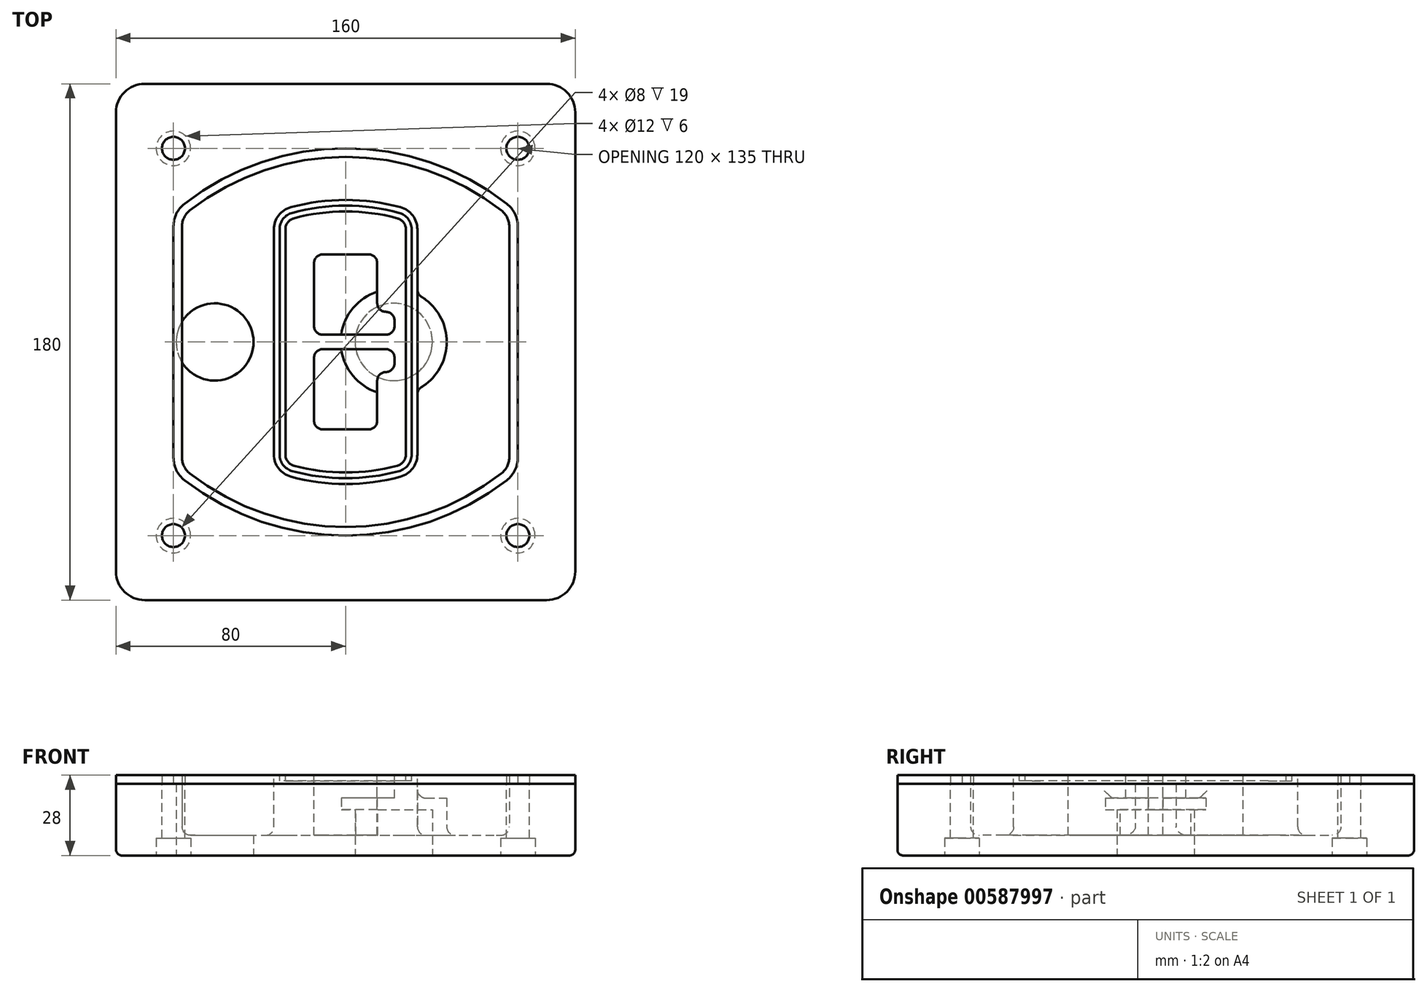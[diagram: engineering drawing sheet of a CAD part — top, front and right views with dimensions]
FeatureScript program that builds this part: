
annotation { "Feature Type Name" : "Feature", "Feature Type Description" : "" }
export const myFeature = defineFeature(function(context is Context, id is Id, definition is map)
    precondition{}
    {
        {
            var Q0;
            Q0=qCreatedBy(makeId("Top.planeOp"),FACE);
            var sketch = newSketch(context, id + "F0", { "sketchPlane" : qUnion([Q0])});
            skPoint(sketch, "E0.rect.middle", {"position": v(0, 0) * mm});
            skLineSegment(sketch, "E1.bottom", {"start": v(-70, -90) * mm, "end": v(70, -90) * mm});
            skLineSegment(sketch, "E1.top", {"start": v(-70, 90) * mm, "end": v(70, 90) * mm});
            skLineSegment(sketch, "E1.left", {"start": v(-80, -80) * mm, "end": v(-80, 80) * mm});
            skLineSegment(sketch, "E1.right", {"start": v(80, -80) * mm, "end": v(80, 80) * mm});
            skLineSegment(sketch, "E2", {"start": v(-80, 90) * mm, "end": v(80, -90) * mm, "construction": true});
            skLineSegment(sketch, "E3", {"start": v(80, 90) * mm, "end": v(-80, -90) * mm, "construction": true});
            skCircle(sketch, "E4", {"center": v(-60, 67.5) * mm, "radius": 4 * mm});
            skCircle(sketch, "E5", {"center": v(60, 67.5) * mm, "radius": 4 * mm});
            skCircle(sketch, "E6", {"center": v(60, -67.5) * mm, "radius": 4 * mm});
            skCircle(sketch, "E7", {"center": v(-60, -67.5) * mm, "radius": 4 * mm});
            skLineSegment(sketch, "E8", {"start": v(-60, 67.5) * mm, "end": v(60, 67.5) * mm, "construction": true});
            skLineSegment(sketch, "E9", {"start": v(60, 67.5) * mm, "end": v(60, -67.5) * mm, "construction": true});
            skLineSegment(sketch, "E10", {"start": v(60, -67.5) * mm, "end": v(-60, -67.5) * mm, "construction": true});
            skLineSegment(sketch, "E11", {"start": v(-60, -67.5) * mm, "end": v(-60, 67.5) * mm, "construction": true});
            skLineSegment(sketch, "E12", {"start": v(-60, 40.3) * mm, "end": v(-60, -40.3) * mm});
            skLineSegment(sketch, "E13", {"start": v(60, 40.3) * mm, "end": v(60, -40.3) * mm});
            skArc(sketch, "E14", {"start": v(56.15, 48.18) * mm, "mid": v(0, 67.5) * mm, "end": v(-56.15, 48.18) * mm});
            skArc(sketch, "E15", {"start": v(-56.15, -48.18) * mm, "mid": v(0, -67.5) * mm, "end": v(56.15, -48.18) * mm});
            skLineSegment(sketch, "E16", {"start": v(-60, 0) * mm, "end": v(60, 0) * mm, "construction": true});
            skPoint(sketch, "E17.visualSharp", {"position": v(-60, -45) * mm});
            skArc(sketch, "E17.filletArc", {"start": v(-60, -40.3) * mm, "mid": v(-58.99, -44.68) * mm, "end": v(-56.15, -48.18) * mm});
            skPoint(sketch, "E18.visualSharp", {"position": v(-60, 45) * mm});
            skArc(sketch, "E18.filletArc", {"start": v(-56.15, 48.18) * mm, "mid": v(-58.99, 44.68) * mm, "end": v(-60, 40.3) * mm});
            skPoint(sketch, "E19.visualSharp", {"position": v(60, 45) * mm});
            skArc(sketch, "E19.filletArc", {"start": v(60, 40.3) * mm, "mid": v(58.99, 44.68) * mm, "end": v(56.15, 48.18) * mm});
            skPoint(sketch, "E20.visualSharp", {"position": v(60, -45) * mm});
            skArc(sketch, "E20.filletArc", {"start": v(56.15, -48.18) * mm, "mid": v(58.99, -44.68) * mm, "end": v(60, -40.3) * mm});
            skPoint(sketch, "E21.visualSharp", {"position": v(-80, 90) * mm});
            skArc(sketch, "E21.filletArc", {"start": v(-70, 90) * mm, "mid": v(-77.07, 87.07) * mm, "end": v(-80, 80) * mm});
            skPoint(sketch, "E22.visualSharp", {"position": v(80, 90) * mm});
            skArc(sketch, "E22.filletArc", {"start": v(80, 80) * mm, "mid": v(77.07, 87.07) * mm, "end": v(70, 90) * mm});
            skPoint(sketch, "E23.visualSharp", {"position": v(80, -90) * mm});
            skArc(sketch, "E23.filletArc", {"start": v(70, -90) * mm, "mid": v(77.07, -87.07) * mm, "end": v(80, -80) * mm});
            skPoint(sketch, "E24.visualSharp", {"position": v(-80, -90) * mm});
            skArc(sketch, "E24.filletArc", {"start": v(-80, -80) * mm, "mid": v(-77.07, -87.07) * mm, "end": v(-70, -90) * mm});
            skArc(sketch, "E25.0", {"start": v(57, 40.3) * mm, "mid": v(56.3, 43.36) * mm, "end": v(54.3, 45.81) * mm});
            skLineSegment(sketch, "E25.1", {"start": v(57, 40.3) * mm, "end": v(57, -40.3) * mm});
            skArc(sketch, "E25.2", {"start": v(54.3, -45.81) * mm, "mid": v(56.3, -43.36) * mm, "end": v(57, -40.3) * mm});
            skArc(sketch, "E25.3", {"start": v(-54.3, -45.81) * mm, "mid": v(0, -64.5) * mm, "end": v(54.3, -45.81) * mm});
            skArc(sketch, "E25.4", {"start": v(-57, -40.3) * mm, "mid": v(-56.3, -43.36) * mm, "end": v(-54.3, -45.81) * mm});
            skArc(sketch, "E25.5", {"start": v(54.3, 45.81) * mm, "mid": v(0, 64.5) * mm, "end": v(-54.3, 45.81) * mm});
            skLineSegment(sketch, "E25.6", {"start": v(-57, 40.3) * mm, "end": v(-57, -40.3) * mm});
            skArc(sketch, "E25.7", {"start": v(-54.3, 45.81) * mm, "mid": v(-56.3, 43.36) * mm, "end": v(-57, 40.3) * mm});
            skArc(sketch, "E26.0", {"start": v(-58.62, 51.33) * mm, "mid": v(-62.58, 46.43) * mm, "end": v(-64, 40.3) * mm});
            skArc(sketch, "E26.1", {"start": v(58.62, 51.33) * mm, "mid": v(0, 71.5) * mm, "end": v(-58.62, 51.33) * mm});
            skArc(sketch, "E26.2", {"start": v(64, 40.3) * mm, "mid": v(62.58, 46.43) * mm, "end": v(58.62, 51.33) * mm});
            skLineSegment(sketch, "E26.3", {"start": v(64, 40.3) * mm, "end": v(64, -40.3) * mm});
            skArc(sketch, "E26.4", {"start": v(58.62, -51.33) * mm, "mid": v(62.58, -46.43) * mm, "end": v(64, -40.3) * mm});
            skLineSegment(sketch, "E26.5", {"start": v(-64, 40.3) * mm, "end": v(-64, -40.3) * mm});
            skArc(sketch, "E26.6", {"start": v(-58.62, -51.33) * mm, "mid": v(0, -71.5) * mm, "end": v(58.62, -51.33) * mm});
            skArc(sketch, "E26.7", {"start": v(-64, -40.3) * mm, "mid": v(-62.58, -46.43) * mm, "end": v(-58.62, -51.33) * mm});
            skSolve(sketch);
        }
        {
            var Q0;
            Q0=makeQuery(id+"F0.imprint","IMPRINT",FACE,{"disambiguationData":[TD([[makeQuery(id+"F0.imprint","IMPRINT",EDGE,{"derivedFrom":sQuery(id+"F0.wireOp",EDGE,"E1.bottom")}),1.0]])]});
            var Q1;
            Q1=makeQuery(id+"F0.imprint","IMPRINT",FACE,{"disambiguationData":[TD([[makeQuery(id+"F0.imprint","IMPRINT",EDGE,{"derivedFrom":sQuery(id+"F0.wireOp",EDGE,"E12")}),1.0]])]});
            var Q2;
            Q2=makeQuery(id+"F0.imprint","IMPRINT",FACE,{"disambiguationData":[TD([[makeQuery(id+"F0.imprint","IMPRINT",EDGE,{"derivedFrom":sQuery(id+"F0.wireOp",EDGE,"E25.0")}),1.0]])]});
            var Q3;
            Q3=makeQuery(id+"F0.imprint","IMPRINT",FACE,{"disambiguationData":[TD([[makeQuery(id+"F0.imprint","IMPRINT",EDGE,{"derivedFrom":sQuery(id+"F0.wireOp",EDGE,"E12")}),-1.0]])]});
            extrude(context, id + "F1", {"entities" : qUnion([Q0, Q1, Q2, Q3]), "oppositeDirection" : true, "depth" : 25 * mm});
        }
        {
            var Q0;
            Q0=makeQuery(id+"F0.imprint","IMPRINT",FACE,{"disambiguationData":[TD([[makeQuery(id+"F0.imprint","IMPRINT",EDGE,{"derivedFrom":sQuery(id+"F0.wireOp",EDGE,"E12")}),1.0]])]});
            extrude(context, id + "F2", {"entities" : qUnion([Q0]), "operationType" : NewBodyOperationType.ADD, "depth" : 3 * mm});
        }
        {
            var Q0;
            Q0=makeQuery(id+"F0.imprint","IMPRINT",FACE,{"disambiguationData":[TD([[makeQuery(id+"F0.imprint","IMPRINT",EDGE,{"derivedFrom":sQuery(id+"F0.wireOp",EDGE,"E25.0")}),1.0]])]});
            extrude(context, id + "F3", {"entities" : qUnion([Q0]), "operationType" : NewBodyOperationType.REMOVE, "oppositeDirection" : true, "depth" : 18 * mm});
        }
        {
            var Q0;
            Q0=makeQuery(id+"F2.opExtrude","CAP_FACE",FACE,{"disambiguationData":[OSD([sQuery(id+"F0.wireOp",EDGE,"E12"),sQuery(id+"F0.wireOp",EDGE,"E13"),sQuery(id+"F0.wireOp",EDGE,"E14"),sQuery(id+"F0.wireOp",EDGE,"E15"),sQuery(id+"F0.wireOp",EDGE,"E17.filletArc"),sQuery(id+"F0.wireOp",EDGE,"E18.filletArc"),sQuery(id+"F0.wireOp",EDGE,"E19.filletArc"),sQuery(id+"F0.wireOp",EDGE,"E20.filletArc"),sQuery(id+"F0.wireOp",EDGE,"E25.0"),sQuery(id+"F0.wireOp",EDGE,"E25.1"),sQuery(id+"F0.wireOp",EDGE,"E25.2"),sQuery(id+"F0.wireOp",EDGE,"E25.3"),sQuery(id+"F0.wireOp",EDGE,"E25.4"),sQuery(id+"F0.wireOp",EDGE,"E25.5"),sQuery(id+"F0.wireOp",EDGE,"E25.6"),sQuery(id+"F0.wireOp",EDGE,"E25.7")])],"isStart":false});
            var sketch = newSketch(context, id + "F4", { "sketchPlane" : qUnion([Q0])});
            skArc(sketch, "E27.0", {"start": v(-19.08, -46.97) * mm, "mid": v(0, -49.5) * mm, "end": v(19.08, -46.97) * mm});
            skArc(sketch, "E28.0", {"start": v(19.08, 46.97) * mm, "mid": v(0, 49.5) * mm, "end": v(-19.08, 46.97) * mm});
            skLineSegment(sketch, "E29", {"start": v(-25, 39.25) * mm, "end": v(-25, -39.25) * mm});
            skLineSegment(sketch, "E30", {"start": v(25, 39.25) * mm, "end": v(25, -39.25) * mm});
            skLineSegment(sketch, "E31", {"start": v(-25, 45.1) * mm, "end": v(25, 45.1) * mm, "construction": true});
            skLineSegment(sketch, "E32", {"start": v(-25, -45.1) * mm, "end": v(25, -45.1) * mm, "construction": true});
            skPoint(sketch, "E33.visualSharp", {"position": v(-25, 45.1) * mm});
            skArc(sketch, "E33.filletArc", {"start": v(-19.08, 46.97) * mm, "mid": v(-23.35, 44.11) * mm, "end": v(-25, 39.25) * mm});
            skPoint(sketch, "E34.visualSharp", {"position": v(25, 45.1) * mm});
            skArc(sketch, "E34.filletArc", {"start": v(25, 39.25) * mm, "mid": v(23.35, 44.11) * mm, "end": v(19.08, 46.97) * mm});
            skPoint(sketch, "E35.visualSharp", {"position": v(25, -45.1) * mm});
            skArc(sketch, "E35.filletArc", {"start": v(19.08, -46.97) * mm, "mid": v(23.35, -44.11) * mm, "end": v(25, -39.25) * mm});
            skPoint(sketch, "E36.visualSharp", {"position": v(-25, -45.1) * mm});
            skArc(sketch, "E36.filletArc", {"start": v(-25, -39.25) * mm, "mid": v(-23.35, -44.11) * mm, "end": v(-19.08, -46.97) * mm});
            skArc(sketch, "E37.0", {"start": v(54.3, 45.81) * mm, "mid": v(0, 64.5) * mm, "end": v(-54.3, 45.81) * mm});
            skArc(sketch, "E37.1", {"start": v(-54.3, 45.81) * mm, "mid": v(-56.3, 43.36) * mm, "end": v(-57, 40.3) * mm});
            skLineSegment(sketch, "E37.2", {"start": v(-57, 40.3) * mm, "end": v(-57, -40.3) * mm});
            skArc(sketch, "E37.3", {"start": v(-57, -40.3) * mm, "mid": v(-56.3, -43.36) * mm, "end": v(-54.3, -45.81) * mm});
            skArc(sketch, "E37.4", {"start": v(-54.3, -45.81) * mm, "mid": v(0, -64.5) * mm, "end": v(54.3, -45.81) * mm});
            skArc(sketch, "E37.5", {"start": v(54.3, -45.81) * mm, "mid": v(56.3, -43.36) * mm, "end": v(57, -40.3) * mm});
            skLineSegment(sketch, "E37.6", {"start": v(57, 40.3) * mm, "end": v(57, -40.3) * mm});
            skArc(sketch, "E37.7", {"start": v(57, 40.3) * mm, "mid": v(56.3, 43.36) * mm, "end": v(54.3, 45.81) * mm});
            skLineSegment(sketch, "E38.0", {"start": v(23, 39.25) * mm, "end": v(23, -39.25) * mm});
            skArc(sketch, "E38.1", {"start": v(18.56, -45.04) * mm, "mid": v(21.76, -42.9) * mm, "end": v(23, -39.25) * mm});
            skArc(sketch, "E38.2", {"start": v(-18.56, -45.04) * mm, "mid": v(0, -47.5) * mm, "end": v(18.56, -45.04) * mm});
            skArc(sketch, "E38.3", {"start": v(-23, -39.25) * mm, "mid": v(-21.76, -42.9) * mm, "end": v(-18.56, -45.04) * mm});
            skLineSegment(sketch, "E38.4", {"start": v(-23, 39.25) * mm, "end": v(-23, -39.25) * mm});
            skArc(sketch, "E38.5", {"start": v(23, 39.25) * mm, "mid": v(21.76, 42.9) * mm, "end": v(18.56, 45.04) * mm});
            skArc(sketch, "E38.6", {"start": v(-18.56, 45.04) * mm, "mid": v(-21.76, 42.9) * mm, "end": v(-23, 39.25) * mm});
            skArc(sketch, "E38.7", {"start": v(18.56, 45.04) * mm, "mid": v(0, 47.5) * mm, "end": v(-18.56, 45.04) * mm});
            skArc(sketch, "E39.0", {"start": v(21, 39.25) * mm, "mid": v(20.18, 41.68) * mm, "end": v(18.04, 43.1) * mm});
            skLineSegment(sketch, "E39.1", {"start": v(21, 39.25) * mm, "end": v(21, -39.25) * mm});
            skArc(sketch, "E39.2", {"start": v(18.04, -43.1) * mm, "mid": v(20.18, -41.68) * mm, "end": v(21, -39.25) * mm});
            skArc(sketch, "E39.3", {"start": v(-18.04, -43.1) * mm, "mid": v(0, -45.5) * mm, "end": v(18.04, -43.1) * mm});
            skArc(sketch, "E39.4", {"start": v(-21, -39.25) * mm, "mid": v(-20.18, -41.68) * mm, "end": v(-18.04, -43.1) * mm});
            skArc(sketch, "E39.5", {"start": v(18.04, 43.1) * mm, "mid": v(0, 45.5) * mm, "end": v(-18.04, 43.1) * mm});
            skLineSegment(sketch, "E39.6", {"start": v(-21, 39.25) * mm, "end": v(-21, -39.25) * mm});
            skArc(sketch, "E39.7", {"start": v(-18.04, 43.1) * mm, "mid": v(-20.18, 41.68) * mm, "end": v(-21, 39.25) * mm});
            skLineSegment(sketch, "E40", {"start": v(-25, 0) * mm, "end": v(25, 0) * mm, "construction": true});
            skLineSegment(sketch, "E41", {"start": v(-11, 5.5) * mm, "end": v(-11, 27.5) * mm});
            skLineSegment(sketch, "E42", {"start": v(-8, 30.5) * mm, "end": v(8, 30.5) * mm});
            skLineSegment(sketch, "E43", {"start": v(11, 27.5) * mm, "end": v(11, 13.5) * mm});
            skLineSegment(sketch, "E44", {"start": v(14, 10.5) * mm, "end": v(14, 10.5) * mm});
            skLineSegment(sketch, "E45", {"start": v(17, 7.5) * mm, "end": v(17, 5.5) * mm});
            skLineSegment(sketch, "E46", {"start": v(14, 2.5) * mm, "end": v(-8, 2.5) * mm});
            skPoint(sketch, "E47.visualSharp", {"position": v(-11, 30.5) * mm});
            skArc(sketch, "E47.filletArc", {"start": v(-8, 30.5) * mm, "mid": v(-10.12, 29.62) * mm, "end": v(-11, 27.5) * mm});
            skPoint(sketch, "E48.visualSharp", {"position": v(11, 30.5) * mm});
            skArc(sketch, "E48.filletArc", {"start": v(11, 27.5) * mm, "mid": v(10.12, 29.62) * mm, "end": v(8, 30.5) * mm});
            skPoint(sketch, "E49.visualSharp", {"position": v(11, 10.5) * mm});
            skArc(sketch, "E49.filletArc", {"start": v(11, 13.5) * mm, "mid": v(11.88, 11.38) * mm, "end": v(14, 10.5) * mm});
            skPoint(sketch, "E50.visualSharp", {"position": v(17, 10.5) * mm});
            skArc(sketch, "E50.filletArc", {"start": v(17, 7.5) * mm, "mid": v(16.12, 9.62) * mm, "end": v(14, 10.5) * mm});
            skPoint(sketch, "E51.visualSharp", {"position": v(17, 2.5) * mm});
            skArc(sketch, "E51.filletArc", {"start": v(14, 2.5) * mm, "mid": v(16.12, 3.38) * mm, "end": v(17, 5.5) * mm});
            skPoint(sketch, "E52.visualSharp", {"position": v(-11, 2.5) * mm});
            skArc(sketch, "E52.filletArc", {"start": v(-11, 5.5) * mm, "mid": v(-10.12, 3.38) * mm, "end": v(-8, 2.5) * mm});
            skLineSegment(sketch, "E53.0.MirrorCS", {"start": v(14, -2.5) * mm, "end": v(-8, -2.5) * mm});
            skArc(sketch, "E54.0.MirrorCS", {"start": v(-11, -5.5) * mm, "mid": v(-10.12, -3.38) * mm, "end": v(-8, -2.5) * mm});
            skLineSegment(sketch, "E55.0.MirrorCS", {"start": v(-11, -5.5) * mm, "end": v(-11, -27.5) * mm});
            skArc(sketch, "E56.0.MirrorCS", {"start": v(-8, -30.5) * mm, "mid": v(-10.12, -29.62) * mm, "end": v(-11, -27.5) * mm});
            skLineSegment(sketch, "E57.0.MirrorCS", {"start": v(-8, -30.5) * mm, "end": v(8, -30.5) * mm});
            skArc(sketch, "E58.0.MirrorCS", {"start": v(11, -27.5) * mm, "mid": v(10.12, -29.62) * mm, "end": v(8, -30.5) * mm});
            skLineSegment(sketch, "E59.0.MirrorCS", {"start": v(11, -27.5) * mm, "end": v(11, -13.5) * mm});
            skArc(sketch, "E60.0.MirrorCS", {"start": v(11, -13.5) * mm, "mid": v(11.88, -11.38) * mm, "end": v(14, -10.5) * mm});
            skArc(sketch, "E61.0.MirrorCS", {"start": v(17, -7.5) * mm, "mid": v(16.12, -9.62) * mm, "end": v(14, -10.5) * mm});
            skLineSegment(sketch, "E62.0.MirrorCS", {"start": v(17, -7.5) * mm, "end": v(17, -5.5) * mm});
            skArc(sketch, "E63.0.MirrorCS", {"start": v(14, -2.5) * mm, "mid": v(16.12, -3.38) * mm, "end": v(17, -5.5) * mm});
            skSolve(sketch);
        }
        {
            var Q0;
            Q0=makeQuery(id+"F4.imprint","IMPRINT",FACE,{"disambiguationData":[TD([[makeQuery(id+"F4.imprint","IMPRINT",EDGE,{"derivedFrom":sQuery(id+"F4.wireOp",EDGE,"E27.0")}),1.0]])]});
            var Q1;
            Q1=makeQuery(id+"F4.imprint","IMPRINT",FACE,{"disambiguationData":[TD([[makeQuery(id+"F4.imprint","IMPRINT",EDGE,{"derivedFrom":sQuery(id+"F4.wireOp",EDGE,"E38.0")}),-1.0]])]});
            var Q2;
            Q2=makeQuery(id+"F4.imprint","IMPRINT",FACE,{"disambiguationData":[TD([[makeQuery(id+"F4.imprint","IMPRINT",EDGE,{"derivedFrom":sQuery(id+"F4.wireOp",EDGE,"E39.0")}),1.0]])]});
            extrude(context, id + "F5", {"entities" : qUnion([Q0, Q1, Q2]), "operationType" : NewBodyOperationType.ADD, "endBound" : BoundingType.UP_TO_NEXT, "oppositeDirection" : true, "depth" : 25 * mm});
        }
        {
            var Q0;
            Q0=makeQuery(id+"F4.imprint","IMPRINT",FACE,{"disambiguationData":[TD([[makeQuery(id+"F4.imprint","IMPRINT",EDGE,{"derivedFrom":sQuery(id+"F4.wireOp",EDGE,"E38.0")}),-1.0]])]});
            extrude(context, id + "F6", {"entities" : qUnion([Q0]), "operationType" : NewBodyOperationType.REMOVE, "oppositeDirection" : true, "depth" : 2 * mm});
        }
        {
            var Q0;
            Q0=makeQuery(id+"F1.opExtrude","CAP_FACE",FACE,{"disambiguationData":[OSD([sQuery(id+"F0.wireOp",EDGE,"E1.bottom"),sQuery(id+"F0.wireOp",EDGE,"E1.top"),sQuery(id+"F0.wireOp",EDGE,"E1.left"),sQuery(id+"F0.wireOp",EDGE,"E1.right"),sQuery(id+"F0.wireOp",EDGE,"E4"),sQuery(id+"F0.wireOp",EDGE,"E5"),sQuery(id+"F0.wireOp",EDGE,"E6"),sQuery(id+"F0.wireOp",EDGE,"E7"),sQuery(id+"F0.wireOp",EDGE,"E21.filletArc"),sQuery(id+"F0.wireOp",EDGE,"E22.filletArc"),sQuery(id+"F0.wireOp",EDGE,"E23.filletArc"),sQuery(id+"F0.wireOp",EDGE,"E24.filletArc")])],"isStart":false});
            var sketch = newSketch(context, id + "F7", { "sketchPlane" : qUnion([Q0])});
            skCircle(sketch, "E64", {"center": v(16.76, 0) * mm, "radius": 13.47 * mm});
            skCircle(sketch, "E65", {"center": v(-45.56, 0) * mm, "radius": 13.47 * mm});
            skLineSegment(sketch, "E66", {"start": v(80, 0) * mm, "end": v(-80, 0) * mm});
            skCircle(sketch, "E67", {"center": v(16.76, 0) * mm, "radius": 18.47 * mm});
            skCircle(sketch, "E68", {"center": v(60, -67.5) * mm, "radius": 6 * mm});
            skCircle(sketch, "E69", {"center": v(-60, -67.5) * mm, "radius": 6 * mm});
            skCircle(sketch, "E70", {"center": v(-60, 67.5) * mm, "radius": 6 * mm});
            skCircle(sketch, "E71", {"center": v(60, 67.5) * mm, "radius": 6 * mm});
            skSolve(sketch);
        }
        {
            var Q0;
            {var subQ1=sQuery(id+"F7.wireOp",EDGE,"E66");var subQ4=sQuery(id+"F7.wireOp",EDGE,"E64");var subQ6=makeQuery(id+"F7.imprint","INTERSECT",VERTEX,{"disambiguationData":[OD(0.0)],"derivedFrom":[subQ4,subQ1]});Q0=makeQuery(id+"F7.imprint","IMPRINT",FACE,{"disambiguationData":[TD([[makeQuery(id+"F7.imprint","IMPRINT",EDGE,{"disambiguationData":[TD([[subQ6,-1.0]])],"derivedFrom":subQ4}),-1.0]])]});}
            var Q1;
            {var subQ0=sQuery(id+"F7.wireOp",EDGE,"E66");var subQ1=sQuery(id+"F7.wireOp",EDGE,"E64");var subQ3=makeQuery(id+"F7.imprint","INTERSECT",VERTEX,{"disambiguationData":[OD(0.0)],"derivedFrom":[subQ1,subQ0]});Q1=makeQuery(id+"F7.imprint","IMPRINT",FACE,{"disambiguationData":[TD([[makeQuery(id+"F7.imprint","IMPRINT",EDGE,{"disambiguationData":[TD([[subQ3,-1.0]])],"derivedFrom":subQ1}),1.0]])]});}
            var Q2;
            {var subQ0=sQuery(id+"F7.wireOp",EDGE,"E66");var subQ1=sQuery(id+"F7.wireOp",EDGE,"E64");var subQ3=makeQuery(id+"F7.imprint","INTERSECT",VERTEX,{"disambiguationData":[OD(0.0)],"derivedFrom":[subQ1,subQ0]});Q2=makeQuery(id+"F7.imprint","IMPRINT",FACE,{"disambiguationData":[TD([[makeQuery(id+"F7.imprint","IMPRINT",EDGE,{"disambiguationData":[TD([[subQ3,1.0]])],"derivedFrom":subQ1}),1.0]])]});}
            var Q3;
            {var subQ1=sQuery(id+"F7.wireOp",EDGE,"E66");var subQ4=sQuery(id+"F7.wireOp",EDGE,"E64");var subQ6=makeQuery(id+"F7.imprint","INTERSECT",VERTEX,{"disambiguationData":[OD(0.0)],"derivedFrom":[subQ4,subQ1]});Q3=makeQuery(id+"F7.imprint","IMPRINT",FACE,{"disambiguationData":[TD([[makeQuery(id+"F7.imprint","IMPRINT",EDGE,{"disambiguationData":[TD([[subQ6,1.0]])],"derivedFrom":subQ4}),-1.0]])]});}
            extrude(context, id + "F8", {"entities" : qUnion([Q0, Q1, Q2, Q3]), "operationType" : NewBodyOperationType.ADD, "oppositeDirection" : true, "depth" : 20 * mm});
        }
        {
            var Q0;
            {var subQ0=sQuery(id+"F7.wireOp",EDGE,"E66");var subQ1=sQuery(id+"F7.wireOp",EDGE,"E64");var subQ3=makeQuery(id+"F7.imprint","INTERSECT",VERTEX,{"disambiguationData":[OD(0.0)],"derivedFrom":[subQ1,subQ0]});Q0=makeQuery(id+"F7.imprint","IMPRINT",FACE,{"disambiguationData":[TD([[makeQuery(id+"F7.imprint","IMPRINT",EDGE,{"disambiguationData":[TD([[subQ3,-1.0]])],"derivedFrom":subQ1}),1.0]])]});}
            var Q1;
            {var subQ0=sQuery(id+"F7.wireOp",EDGE,"E66");var subQ1=sQuery(id+"F7.wireOp",EDGE,"E64");var subQ3=makeQuery(id+"F7.imprint","INTERSECT",VERTEX,{"disambiguationData":[OD(0.0)],"derivedFrom":[subQ1,subQ0]});Q1=makeQuery(id+"F7.imprint","IMPRINT",FACE,{"disambiguationData":[TD([[makeQuery(id+"F7.imprint","IMPRINT",EDGE,{"disambiguationData":[TD([[subQ3,1.0]])],"derivedFrom":subQ1}),1.0]])]});}
            extrude(context, id + "F9", {"entities" : qUnion([Q0, Q1]), "operationType" : NewBodyOperationType.REMOVE, "oppositeDirection" : true, "depth" : 16 * mm});
        }
        {
            var Q0;
            {var subQ0=sQuery(id+"F7.wireOp",EDGE,"E66");var subQ1=sQuery(id+"F7.wireOp",EDGE,"E65");var subQ3=makeQuery(id+"F7.imprint","INTERSECT",VERTEX,{"disambiguationData":[OD(0.0)],"derivedFrom":[subQ1,subQ0]});Q0=makeQuery(id+"F7.imprint","IMPRINT",FACE,{"disambiguationData":[TD([[makeQuery(id+"F7.imprint","IMPRINT",EDGE,{"disambiguationData":[TD([[subQ3,-1.0]])],"derivedFrom":subQ1}),1.0]])]});}
            var Q1;
            {var subQ0=sQuery(id+"F7.wireOp",EDGE,"E66");var subQ1=sQuery(id+"F7.wireOp",EDGE,"E65");var subQ3=makeQuery(id+"F7.imprint","INTERSECT",VERTEX,{"disambiguationData":[OD(0.0)],"derivedFrom":[subQ1,subQ0]});Q1=makeQuery(id+"F7.imprint","IMPRINT",FACE,{"disambiguationData":[TD([[makeQuery(id+"F7.imprint","IMPRINT",EDGE,{"disambiguationData":[TD([[subQ3,1.0]])],"derivedFrom":subQ1}),1.0]])]});}
            extrude(context, id + "F10", {"entities" : qUnion([Q0, Q1]), "operationType" : NewBodyOperationType.REMOVE, "oppositeDirection" : true, "depth" : 25 * mm});
        }
        {
            var Q0;
            Q0=makeQuery(id+"F7.imprint","IMPRINT",FACE,{"disambiguationData":[TD([[makeQuery(id+"F7.imprint","IMPRINT",EDGE,{"derivedFrom":sQuery(id+"F7.wireOp",EDGE,"E68")}),1.0]])]});
            var Q1;
            Q1=makeQuery(id+"F7.imprint","IMPRINT",FACE,{"disambiguationData":[TD([[makeQuery(id+"F7.imprint","IMPRINT",EDGE,{"derivedFrom":makeQuery(id+"F1.opExtrude","CAP_EDGE",EDGE,{"disambiguationData":[OSD([sQuery(id+"F0.wireOp",EDGE,"E5")])],"isStart":false})}),-1.0]])]});
            var Q2;
            Q2=makeQuery(id+"F7.imprint","IMPRINT",FACE,{"disambiguationData":[TD([[makeQuery(id+"F7.imprint","IMPRINT",EDGE,{"derivedFrom":sQuery(id+"F7.wireOp",EDGE,"E69")}),1.0]])]});
            var Q3;
            Q3=makeQuery(id+"F7.imprint","IMPRINT",FACE,{"disambiguationData":[TD([[makeQuery(id+"F7.imprint","IMPRINT",EDGE,{"derivedFrom":makeQuery(id+"F1.opExtrude","CAP_EDGE",EDGE,{"disambiguationData":[OSD([sQuery(id+"F0.wireOp",EDGE,"E4")])],"isStart":false})}),-1.0]])]});
            var Q4;
            Q4=makeQuery(id+"F7.imprint","IMPRINT",FACE,{"disambiguationData":[TD([[makeQuery(id+"F7.imprint","IMPRINT",EDGE,{"derivedFrom":sQuery(id+"F7.wireOp",EDGE,"E70")}),1.0]])]});
            var Q5;
            Q5=makeQuery(id+"F7.imprint","IMPRINT",FACE,{"disambiguationData":[TD([[makeQuery(id+"F7.imprint","IMPRINT",EDGE,{"derivedFrom":makeQuery(id+"F1.opExtrude","CAP_EDGE",EDGE,{"disambiguationData":[OSD([sQuery(id+"F0.wireOp",EDGE,"E7")])],"isStart":false})}),-1.0]])]});
            var Q6;
            Q6=makeQuery(id+"F7.imprint","IMPRINT",FACE,{"disambiguationData":[TD([[makeQuery(id+"F7.imprint","IMPRINT",EDGE,{"derivedFrom":sQuery(id+"F7.wireOp",EDGE,"E71")}),1.0]])]});
            var Q7;
            Q7=makeQuery(id+"F7.imprint","IMPRINT",FACE,{"disambiguationData":[TD([[makeQuery(id+"F7.imprint","IMPRINT",EDGE,{"derivedFrom":makeQuery(id+"F1.opExtrude","CAP_EDGE",EDGE,{"disambiguationData":[OSD([sQuery(id+"F0.wireOp",EDGE,"E6")])],"isStart":false})}),-1.0]])]});
            extrude(context, id + "F11", {"entities" : qUnion([Q0, Q1, Q2, Q3, Q4, Q5, Q6, Q7]), "operationType" : NewBodyOperationType.REMOVE, "oppositeDirection" : true, "depth" : 6 * mm});
        }
        {
            var Q0;
            Q0=makeQuery(id+"F9.boolean.opBoolean","COPY",FACE,{"derivedFrom":makeQuery(id+"F9.opExtrude","CAP_FACE",FACE,{"disambiguationData":[OSD([sQuery(id+"F7.wireOp",EDGE,"E64")])],"isStart":false})});
            var sketch = newSketch(context, id + "F12", { "sketchPlane" : qUnion([Q0])});
            skArc(sketch, "E72.0", {"start": v(11, 17.55) * mm, "mid": v(2.57, 11.82) * mm, "end": v(-1.54, 2.5) * mm});
            skArc(sketch, "E72.1", {"start": v(-1.54, -2.5) * mm, "mid": v(2.57, -11.82) * mm, "end": v(11, -17.55) * mm});
            skLineSegment(sketch, "E73", {"start": v(-1.54, -2.5) * mm, "end": v(14, -2.5) * mm});
            skLineSegment(sketch, "E74.0", {"start": v(14, 2.5) * mm, "end": v(-1.54, 2.5) * mm});
            skArc(sketch, "E74.1", {"start": v(14, 2.5) * mm, "mid": v(16.12, 3.38) * mm, "end": v(17, 5.5) * mm});
            skLineSegment(sketch, "E74.2", {"start": v(17, 7.5) * mm, "end": v(17, 5.5) * mm});
            skArc(sketch, "E74.3", {"start": v(17, 7.5) * mm, "mid": v(16.12, 9.62) * mm, "end": v(14, 10.5) * mm});
            skArc(sketch, "E74.4", {"start": v(11, 13.5) * mm, "mid": v(11.88, 11.38) * mm, "end": v(14, 10.5) * mm});
            skLineSegment(sketch, "E74.5", {"start": v(11, 17.55) * mm, "end": v(11, 13.5) * mm});
            skLineSegment(sketch, "E74.7", {"start": v(14, -2.5) * mm, "end": v(-1.54, -2.5) * mm});
            skArc(sketch, "E74.8", {"start": v(14, -2.5) * mm, "mid": v(16.12, -3.38) * mm, "end": v(17, -5.5) * mm});
            skLineSegment(sketch, "E74.9", {"start": v(17, -7.5) * mm, "end": v(17, -5.5) * mm});
            skArc(sketch, "E74.10", {"start": v(17, -7.5) * mm, "mid": v(16.12, -9.62) * mm, "end": v(14, -10.5) * mm});
            skArc(sketch, "E74.11", {"start": v(11, -13.5) * mm, "mid": v(11.88, -11.38) * mm, "end": v(14, -10.5) * mm});
            skLineSegment(sketch, "E74.12", {"start": v(11, -17.55) * mm, "end": v(11, -13.5) * mm});
            skPoint(sketch, "E75.orphan", {"position": v(11, -27.5) * mm});
            skPoint(sketch, "E76.orphan", {"position": v(-8, -2.5) * mm});
            skPoint(sketch, "E77.orphan", {"position": v(-8, 2.5) * mm});
            skPoint(sketch, "E78.orphan", {"position": v(11, 27.5) * mm});
            skSolve(sketch);
        }
        {
            var Q0;
            {var subQ7=sQuery(id+"F12.wireOp",EDGE,"E72.0");var subQ14=sQuery(id+"F12.wireOp",EDGE,"E72.1");var subQ16=sQuery(id+"F12.wireOp",EDGE,"E74.1");var subQ18=sQuery(id+"F12.wireOp",EDGE,"E74.8");Q0=qUnion([makeQuery(id+"F12.imprint","IMPRINT",FACE,{"disambiguationData":[TD([[makeQuery(id+"F12.imprint","IMPRINT",EDGE,{"derivedFrom":subQ7}),1.0]])]}),makeQuery(id+"F12.imprint","IMPRINT",FACE,{"disambiguationData":[TD([[makeQuery(id+"F12.imprint","IMPRINT",EDGE,{"derivedFrom":subQ14}),1.0]])]}),makeQuery(id+"F12.imprint","IMPRINT",FACE,{"disambiguationData":[TD([[makeQuery(id+"F12.imprint","IMPRINT",EDGE,{"derivedFrom":subQ16}),1.0]])]}),makeQuery(id+"F12.imprint","IMPRINT",FACE,{"disambiguationData":[TD([[makeQuery(id+"F12.imprint","IMPRINT",EDGE,{"derivedFrom":subQ18}),-1.0]])]})]);}
            var Q1;
            Q1=makeQuery(id+"F5.boolean.opBoolean","SPLIT",FACE,{"disambiguationData":[TD([makeQuery(id+"F5.opExtrude","SWEPT_FACE",FACE,{"disambiguationData":[OSD([sQuery(id+"F4.wireOp",EDGE,"E41")])]})])],"derivedFrom":makeQuery(id+"F3.boolean.opBoolean","COPY",FACE,{"derivedFrom":makeQuery(id+"F3.opExtrude","CAP_FACE",FACE,{"disambiguationData":[OSD([sQuery(id+"F0.wireOp",EDGE,"E25.0"),sQuery(id+"F0.wireOp",EDGE,"E25.1"),sQuery(id+"F0.wireOp",EDGE,"E25.2"),sQuery(id+"F0.wireOp",EDGE,"E25.3"),sQuery(id+"F0.wireOp",EDGE,"E25.4"),sQuery(id+"F0.wireOp",EDGE,"E25.5"),sQuery(id+"F0.wireOp",EDGE,"E25.6"),sQuery(id+"F0.wireOp",EDGE,"E25.7")])],"isStart":false})})});
            extrude(context, id + "F13", {"entities" : qUnion([Q0]), "operationType" : NewBodyOperationType.REMOVE, "endBound" : BoundingType.UP_TO_SURFACE, "endBoundEntityFace" : qUnion([Q1]), "depth" : 25 * mm});
        }
        {
            var Q0;
            Q0=makeQuery(id+"F3.boolean.opBoolean","COPY",EDGE,{"derivedFrom":makeQuery(id+"F3.opExtrude","CAP_EDGE",EDGE,{"disambiguationData":[OSD([sQuery(id+"F0.wireOp",EDGE,"E25.6")])],"isStart":false})});
            var Q1;
            Q1=makeQuery(id+"F8.boolean.opBoolean","INTERSECT",EDGE,{"derivedFrom":[makeQuery(id+"F5.opExtrude","SWEPT_FACE",FACE,{"disambiguationData":[OSD([sQuery(id+"F4.wireOp",EDGE,"E30")])]}),makeQuery(id+"F8.opExtrude","CAP_FACE",FACE,{"disambiguationData":[OSD([sQuery(id+"F7.wireOp",EDGE,"E67")])],"isStart":false})]});
            var Q2;
            Q2=makeQuery(id+"F8.boolean.opBoolean","INTERSECT",EDGE,{"disambiguationData":[OD(1.0)],"derivedFrom":[makeQuery(id+"F5.opExtrude","SWEPT_FACE",FACE,{"disambiguationData":[OSD([sQuery(id+"F4.wireOp",EDGE,"E30")])]}),makeQuery(id+"F8.opExtrude","SWEPT_FACE",FACE,{"disambiguationData":[OSD([sQuery(id+"F7.wireOp",EDGE,"E67")])]})]});
            var Q3;
            {var subQ0=sQuery(id+"F4.wireOp",EDGE,"E30");Q3=makeQuery(id+"F8.boolean.opBoolean","SPLIT",EDGE,{"disambiguationData":[TD([makeQuery(id+"F5.opExtrude","SWEPT_FACE",FACE,{"disambiguationData":[OSD([sQuery(id+"F4.wireOp",EDGE,"E35.filletArc")])]})])],"derivedFrom":makeQuery(id+"F5.opExtrude","CAP_EDGE",EDGE,{"disambiguationData":[OSD([subQ0])],"isStart":false})});}
            var Q4;
            {var subQ0=sQuery(id+"F0.wireOp",EDGE,"E25.7");var subQ1=sQuery(id+"F0.wireOp",EDGE,"E25.1");var subQ2=sQuery(id+"F0.wireOp",EDGE,"E25.6");var subQ3=sQuery(id+"F0.wireOp",EDGE,"E25.5");var subQ4=sQuery(id+"F0.wireOp",EDGE,"E25.4");var subQ5=sQuery(id+"F0.wireOp",EDGE,"E25.0");var subQ6=sQuery(id+"F0.wireOp",EDGE,"E25.2");var subQ7=sQuery(id+"F0.wireOp",EDGE,"E25.3");Q4=makeQuery(id+"F8.boolean.opBoolean","INTERSECT",EDGE,{"derivedFrom":[makeQuery(id+"F5.boolean.opBoolean","SPLIT",FACE,{"disambiguationData":[TD([makeQuery(id+"F2.opExtrude","SWEPT_FACE",FACE,{"disambiguationData":[OSD([subQ5])]})])],"derivedFrom":makeQuery(id+"F3.boolean.opBoolean","COPY",FACE,{"derivedFrom":makeQuery(id+"F3.opExtrude","CAP_FACE",FACE,{"disambiguationData":[OSD([subQ5,subQ1,subQ6,subQ7,subQ4,subQ3,subQ2,subQ0])],"isStart":false})})}),makeQuery(id+"F8.opExtrude","SWEPT_FACE",FACE,{"disambiguationData":[OSD([sQuery(id+"F7.wireOp",EDGE,"E67")])]})]});}
            var Q5;
            Q5=makeQuery(id+"F8.boolean.opBoolean","INTERSECT",EDGE,{"disambiguationData":[OD(0.0)],"derivedFrom":[makeQuery(id+"F5.opExtrude","SWEPT_FACE",FACE,{"disambiguationData":[OSD([sQuery(id+"F4.wireOp",EDGE,"E30")])]}),makeQuery(id+"F8.opExtrude","SWEPT_FACE",FACE,{"disambiguationData":[OSD([sQuery(id+"F7.wireOp",EDGE,"E67")])]})]});
            fillet(context, id + "F14", {"entities" : qUnion([Q0, Q1, Q2, Q3, Q4, Q5]), "radius" : 3 * mm, "tangentPropagation" : true, "allowEdgeOverflow" : false});
        }
        {
            var Q0;
            Q0=makeQuery(id+"F1.opExtrude","CAP_EDGE",EDGE,{"disambiguationData":[OSD([sQuery(id+"F0.wireOp",EDGE,"E1.bottom")])],"isStart":false});
            fillet(context, id + "F15", {"entities" : qUnion([Q0]), "radius" : 2 * mm, "tangentPropagation" : true, "allowEdgeOverflow" : false});
        }
        {
            var Q0;
            {var subQ0=sQuery(id+"F0.wireOp",EDGE,"E21.filletArc");var subQ1=sQuery(id+"F0.wireOp",EDGE,"E7");var subQ2=sQuery(id+"F0.wireOp",EDGE,"E6");var subQ3=sQuery(id+"F0.wireOp",EDGE,"E5");var subQ4=sQuery(id+"F0.wireOp",EDGE,"E4");var subQ5=sQuery(id+"F0.wireOp",EDGE,"E22.filletArc");var subQ6=sQuery(id+"F0.wireOp",EDGE,"E1.bottom");var subQ7=sQuery(id+"F0.wireOp",EDGE,"E1.right");var subQ8=sQuery(id+"F0.wireOp",EDGE,"E1.top");var subQ9=sQuery(id+"F0.wireOp",EDGE,"E1.left");var subQ10=sQuery(id+"F0.wireOp",EDGE,"E23.filletArc");var subQ11=sQuery(id+"F0.wireOp",EDGE,"E24.filletArc");Q0=makeQuery(id+"F2.boolean.opBoolean","SPLIT",FACE,{"disambiguationData":[TD([makeQuery(id+"F1.opExtrude","SWEPT_FACE",FACE,{"disambiguationData":[OSD([subQ6])]})])],"derivedFrom":makeQuery(id+"F1.opExtrude","CAP_FACE",FACE,{"disambiguationData":[OSD([subQ6,subQ8,subQ9,subQ7,subQ4,subQ3,subQ2,subQ1,subQ0,subQ5,subQ10,subQ11])],"isStart":true})});}
            var sketch = newSketch(context, id + "F16", { "sketchPlane" : qUnion([Q0])});
            skCircle(sketch, "E79", {"center": v(0, 120) * mm, "radius": 6 * mm});
            skLineSegment(sketch, "E80", {"start": v(-32.24, 90) * mm, "end": v(-15, 108) * mm});
            skLineSegment(sketch, "E81", {"start": v(-15, 108) * mm, "end": v(-15, 120) * mm});
            skArc(sketch, "E82", {"start": v(15, 120) * mm, "mid": v(0, 135) * mm, "end": v(-15, 120) * mm});
            skLineSegment(sketch, "E83", {"start": v(15, 120) * mm, "end": v(15, 108) * mm});
            skLineSegment(sketch, "E84", {"start": v(15, 108) * mm, "end": v(33, 90) * mm});
            skLineSegment(sketch, "E85", {"start": v(0, 120) * mm, "end": v(0, 90) * mm, "construction": true});
            skLineSegment(sketch, "E86", {"start": v(-80, 0) * mm, "end": v(80, 0) * mm, "construction": true});
            skLineSegment(sketch, "E87.MirrorCS", {"start": v(32.24, 90) * mm, "end": v(15, 108) * mm});
            skLineSegment(sketch, "E88.MirrorCS", {"start": v(-15, 108) * mm, "end": v(-33, 90) * mm});
            skLineSegment(sketch, "E89.MirrorCS", {"start": v(-15, 120) * mm, "end": v(-15, 108) * mm});
            skArc(sketch, "E90.MirrorCS", {"start": v(-15, 120) * mm, "mid": v(0, 135) * mm, "end": v(15, 120) * mm});
            skLineSegment(sketch, "E91.MirrorCS", {"start": v(15, 108) * mm, "end": v(15, 120) * mm});
            skLineSegment(sketch, "E92.MirrorCS", {"start": v(80, 0) * mm, "end": v(-80, 0) * mm, "construction": true});
            skLineSegment(sketch, "E93.MirrorCS", {"start": v(15, -108) * mm, "end": v(15, -120) * mm});
            skArc(sketch, "E94.MirrorCS", {"start": v(15, -120) * mm, "mid": v(0, -135) * mm, "end": v(-15, -120) * mm});
            skCircle(sketch, "E95.MirrorC", {"center": v(0, -120) * mm, "radius": 6 * mm});
            skLineSegment(sketch, "E96.MirrorCS", {"start": v(-15, -120) * mm, "end": v(-15, -108) * mm});
            skLineSegment(sketch, "E97.MirrorCS", {"start": v(-15, -108) * mm, "end": v(-15, -120) * mm});
            skLineSegment(sketch, "E98.MirrorCS", {"start": v(15, -120) * mm, "end": v(15, -108) * mm});
            skArc(sketch, "E99.MirrorCS", {"start": v(-15, -120) * mm, "mid": v(0, -135) * mm, "end": v(15, -120) * mm});
            skLineSegment(sketch, "E100.MirrorCS", {"start": v(15, -108) * mm, "end": v(33, -90) * mm});
            skLineSegment(sketch, "E101.MirrorCS", {"start": v(-15, -108) * mm, "end": v(-33, -90) * mm});
            skLineSegment(sketch, "E102.MirrorCS", {"start": v(32.24, -90) * mm, "end": v(15, -108) * mm});
            skLineSegment(sketch, "E103.MirrorCS", {"start": v(-32.24, -90) * mm, "end": v(-15, -108) * mm});
            skLineSegment(sketch, "E104.MirrorCS", {"start": v(0, -120) * mm, "end": v(0, -90) * mm, "construction": true});
            skSolve(sketch);
        }
        {
            var Q0;
            {var subQ0=sQuery(id+"F16.wireOp",EDGE,"E102.MirrorCS");Q0=makeQuery(id+"F16.imprint","IMPRINT",FACE,{"disambiguationData":[TD([[makeQuery(id+"F16.imprint","IMPRINT",EDGE,{"derivedFrom":subQ0}),-1.0]])]});}
            var Q1;
            Q1=makeQuery(id+"F16.imprint","IMPRINT",FACE,{"disambiguationData":[TD([[makeQuery(id+"F16.imprint","IMPRINT",EDGE,{"derivedFrom":makeQuery(id+"F1.opExtrude","CAP_EDGE",EDGE,{"disambiguationData":[OSD([sQuery(id+"F0.wireOp",EDGE,"E1.left")])],"isStart":true})}),-1.0]])]});
            var Q2;
            {var subQ0=sQuery(id+"F16.wireOp",EDGE,"E80");Q2=makeQuery(id+"F16.imprint","IMPRINT",FACE,{"disambiguationData":[TD([[makeQuery(id+"F16.imprint","IMPRINT",EDGE,{"derivedFrom":subQ0}),-1.0]])]});}
            var Q3;
            {var subQ0=sQuery(id+"F4.wireOp",EDGE,"E63.0.MirrorCS");var subQ1=sQuery(id+"F4.wireOp",EDGE,"E62.0.MirrorCS");var subQ2=sQuery(id+"F4.wireOp",EDGE,"E61.0.MirrorCS");var subQ3=sQuery(id+"F4.wireOp",EDGE,"E60.0.MirrorCS");var subQ4=sQuery(id+"F4.wireOp",EDGE,"E59.0.MirrorCS");var subQ5=sQuery(id+"F4.wireOp",EDGE,"E58.0.MirrorCS");var subQ6=sQuery(id+"F4.wireOp",EDGE,"E57.0.MirrorCS");var subQ7=sQuery(id+"F4.wireOp",EDGE,"E56.0.MirrorCS");var subQ8=sQuery(id+"F4.wireOp",EDGE,"E55.0.MirrorCS");var subQ9=sQuery(id+"F4.wireOp",EDGE,"E54.0.MirrorCS");var subQ10=sQuery(id+"F4.wireOp",EDGE,"E53.0.MirrorCS");var subQ11=sQuery(id+"F4.wireOp",EDGE,"E52.filletArc");var subQ12=sQuery(id+"F4.wireOp",EDGE,"E45");var subQ13=sQuery(id+"F4.wireOp",EDGE,"E43");var subQ14=sQuery(id+"F4.wireOp",EDGE,"E42");var subQ15=sQuery(id+"F4.wireOp",EDGE,"E41");var subQ16=sQuery(id+"F4.wireOp",EDGE,"E46");var subQ17=sQuery(id+"F4.wireOp",EDGE,"E47.filletArc");var subQ18=sQuery(id+"F4.wireOp",EDGE,"E48.filletArc");var subQ19=sQuery(id+"F4.wireOp",EDGE,"E49.filletArc");var subQ20=sQuery(id+"F4.wireOp",EDGE,"E50.filletArc");var subQ21=sQuery(id+"F4.wireOp",EDGE,"E51.filletArc");Q3=makeQuery(id+"F6.boolean.opBoolean","SPLIT",FACE,{"disambiguationData":[TD([makeQuery(id+"F5.opExtrude","SWEPT_FACE",FACE,{"disambiguationData":[OSD([subQ15])]})])],"derivedFrom":makeQuery(id+"F5.opExtrude","CAP_FACE",FACE,{"disambiguationData":[OSD([sQuery(id+"F4.wireOp",EDGE,"E27.0"),sQuery(id+"F4.wireOp",EDGE,"E28.0"),sQuery(id+"F4.wireOp",EDGE,"E29"),sQuery(id+"F4.wireOp",EDGE,"E30"),sQuery(id+"F4.wireOp",EDGE,"E33.filletArc"),sQuery(id+"F4.wireOp",EDGE,"E34.filletArc"),sQuery(id+"F4.wireOp",EDGE,"E35.filletArc"),sQuery(id+"F4.wireOp",EDGE,"E36.filletArc"),subQ15,subQ14,subQ13,subQ12,subQ16,subQ17,subQ18,subQ19,subQ20,subQ21,subQ11,subQ10,subQ9,subQ8,subQ7,subQ6,subQ5,subQ4,subQ3,subQ2,subQ1,subQ0])],"isStart":true})});}
            extrude(context, id + "F17", {"entities" : qUnion([Q0, Q1, Q2]), "endBound" : BoundingType.UP_TO_SURFACE, "depth" : 25 * mm, "endBoundEntityFace" : qUnion([Q3]), "offsetDistance" : 25 * mm});
        }
    });
